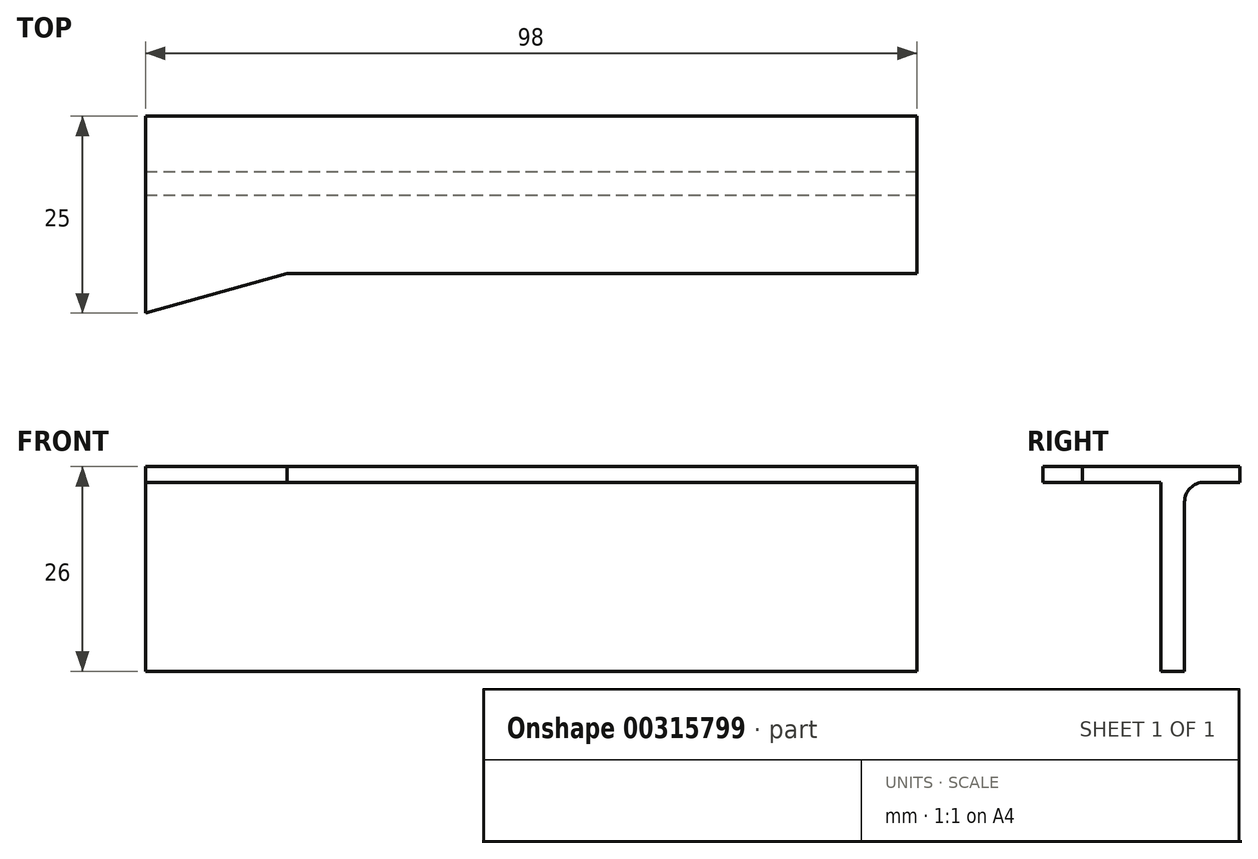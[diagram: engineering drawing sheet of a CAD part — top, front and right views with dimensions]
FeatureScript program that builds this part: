
annotation { "Feature Type Name" : "Feature", "Feature Type Description" : "" }
export const myFeature = defineFeature(function(context is Context, id is Id, definition is map)
    precondition{}
    {
        {
            var Q0;
            Q0=qCreatedBy(makeId("Top.planeOp"),FACE);
            var sketch = newSketch(context, id + "F0", { "sketchPlane" : qUnion([Q0])});
            skLineSegment(sketch, "E0.bottom", {"start": v(0, 0) * mm, "end": v(80, 0) * mm});
            skLineSegment(sketch, "E0.top", {"start": v(0, 20) * mm, "end": v(80, 20) * mm});
            skLineSegment(sketch, "E0.left", {"start": v(0, 0) * mm, "end": v(0, 20) * mm});
            skLineSegment(sketch, "E0.right", {"start": v(80, 0) * mm, "end": v(80, 20) * mm});
            skLineSegment(sketch, "E1", {"start": v(0, 20) * mm, "end": v(-18, 20) * mm});
            skLineSegment(sketch, "E2", {"start": v(-18, 20) * mm, "end": v(-18, -5) * mm});
            skLineSegment(sketch, "E3", {"start": v(-18, -5) * mm, "end": v(0, 0) * mm});
            skSolve(sketch);
        }
        {
            var Q0;
            Q0 = qSketchRegion(id + "F0", true);
            extrude(context, id + "F1", {"entities" : qUnion([Q0]), "depth" : 2 * mm});
        }
        {
            var Q0;
            Q0=makeQuery(id+"F1.opExtrude","CAP_FACE",FACE,{"disambiguationData":[OSD([sQuery(id+"F0.wireOp",EDGE,"E0.bottom"),sQuery(id+"F0.wireOp",EDGE,"E0.top"),sQuery(id+"F0.wireOp",EDGE,"E0.right"),sQuery(id+"F0.wireOp",EDGE,"E1"),sQuery(id+"F0.wireOp",EDGE,"E2"),sQuery(id+"F0.wireOp",EDGE,"E3")])],"isStart":true});
            var sketch = newSketch(context, id + "F2", { "sketchPlane" : qUnion([Q0])});
            skLineSegment(sketch, "E4.bottom", {"start": v(-18, -13) * mm, "end": v(80, -13) * mm});
            skLineSegment(sketch, "E4.top", {"start": v(-18, -10) * mm, "end": v(80, -10) * mm});
            skLineSegment(sketch, "E4.left", {"start": v(-18, -13) * mm, "end": v(-18, -10) * mm});
            skLineSegment(sketch, "E4.right", {"start": v(80, -13) * mm, "end": v(80, -10) * mm});
            skSolve(sketch);
        }
        {
            var Q0;
            Q0 = qSketchRegion(id + "F2", true);
            extrude(context, id + "F3", {"entities" : qUnion([Q0]), "operationType" : NewBodyOperationType.ADD, "depth" : 24 * mm});
        }
        {
            var Q0;
            Q0=makeQuery(id+"F3.opExtrude","CAP_EDGE",EDGE,{"disambiguationData":[OSD([sQuery(id+"F2.wireOp",EDGE,"E4.top")])],"isStart":true});
            var Q1;
            Q1=makeQuery(id+"F3.opExtrude","CAP_EDGE",EDGE,{"disambiguationData":[OSD([sQuery(id+"F2.wireOp",EDGE,"E4.bottom")])],"isStart":true});
            fillet(context, id + "F4", {"entities" : qUnion([Q0, Q1]), "radius" : 2.5 * mm, "tangentPropagation" : true, "allowEdgeOverflow" : false});
        }
    });
